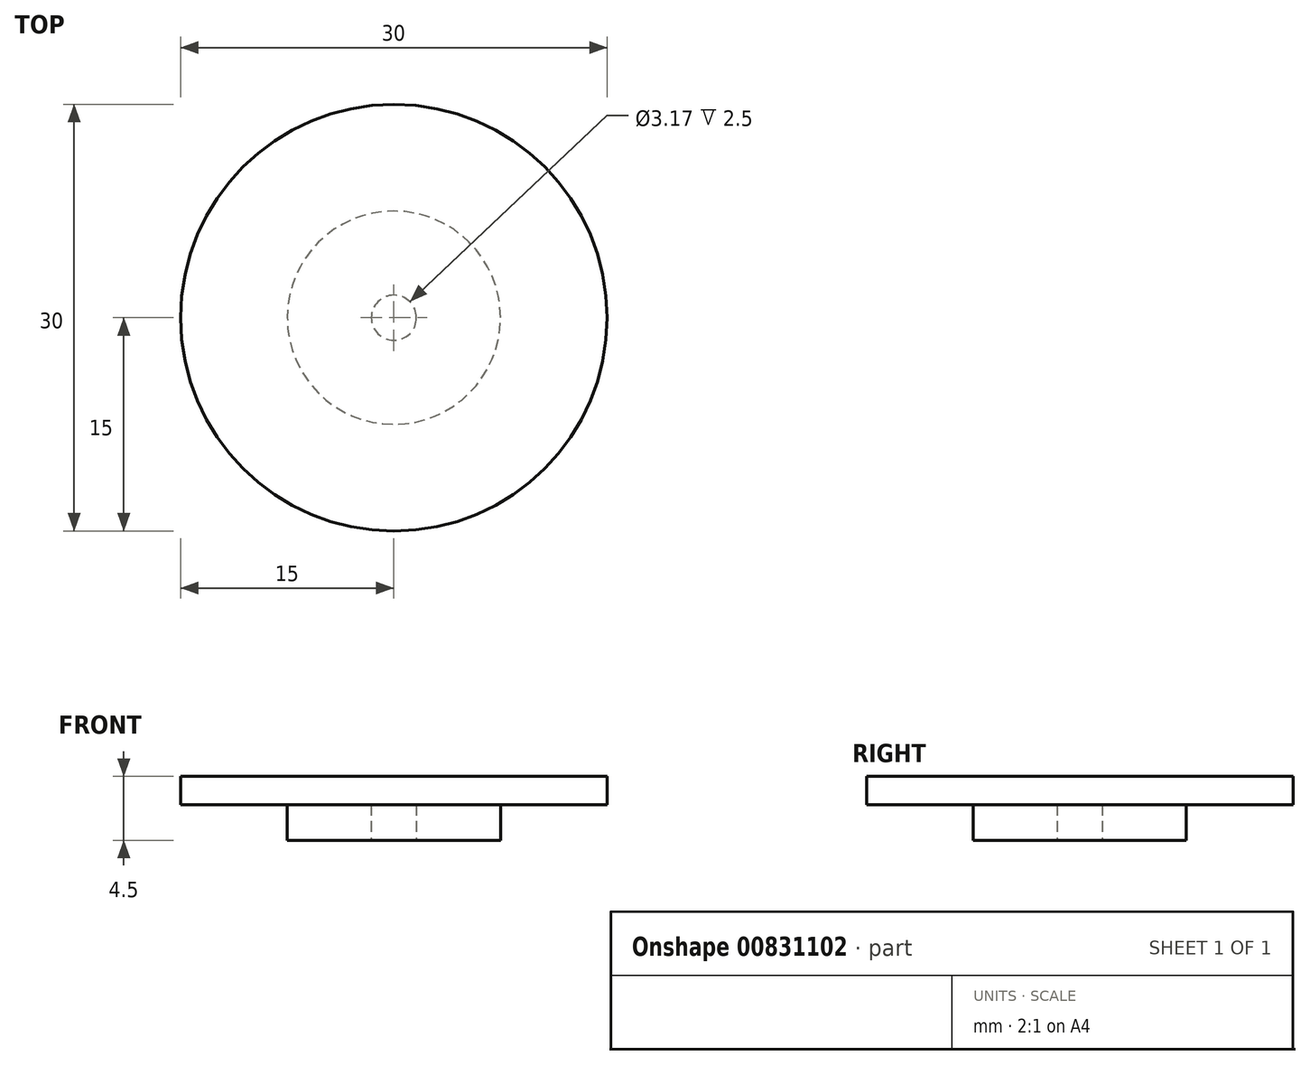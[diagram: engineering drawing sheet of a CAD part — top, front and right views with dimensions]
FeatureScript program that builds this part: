
annotation { "Feature Type Name" : "Feature", "Feature Type Description" : "" }
export const myFeature = defineFeature(function(context is Context, id is Id, definition is map)
    precondition{}
    {
        {
            var Q0;
            Q0=qCreatedBy(makeId("Top.planeOp"),FACE);
            var sketch = newSketch(context, id + "F0", { "sketchPlane" : qUnion([Q0])});
            skCircle(sketch, "E0", {"center": v(0, 0) * mm, "radius": 1.59 * mm});
            skCircle(sketch, "E1", {"center": v(0, 0) * mm, "radius": 7.5 * mm});
            skSolve(sketch);
        }
        {
            var Q0;
            Q0 = qSketchRegion(id + "F0", true);
            var Q1;
            Q1=makeQuery(id+"F0.imprint","IMPRINT",FACE,{"disambiguationData":[TD([[makeQuery(id+"F0.imprint","IMPRINT",EDGE,{"derivedFrom":sQuery(id+"F0.wireOp",EDGE,"E0")}),-1.0]])]});
            extrude(context, id + "F1", {"entities" : qUnion([Q0, Q1]), "depth" : 2.5 * mm, "offsetDistance" : 25.4 * mm});
        }
        {
            var Q0;
            Q0=makeQuery(id+"F1.opExtrude","CAP_FACE",FACE,{"disambiguationData":[OSD([sQuery(id+"F0.wireOp",EDGE,"E0"),sQuery(id+"F0.wireOp",EDGE,"E1")])],"isStart":false});
            var sketch = newSketch(context, id + "F2", { "sketchPlane" : qUnion([Q0])});
            skCircle(sketch, "E2", {"center": v(0, 0) * mm, "radius": 15 * mm});
            skSolve(sketch);
        }
        {
            var Q0;
            Q0 = qSketchRegion(id + "F2", true);
            var Q1;
            Q1=makeQuery(id+"F2.imprint","IMPRINT",FACE,{"disambiguationData":[TD([[makeQuery(id+"F2.imprint","IMPRINT",EDGE,{"derivedFrom":sQuery(id+"F2.wireOp",EDGE,"E2")}),1.0]])]});
            extrude(context, id + "F3", {"entities" : qUnion([Q0, Q1]), "operationType" : NewBodyOperationType.ADD, "depth" : 2 * mm, "offsetDistance" : 25.4 * mm});
        }
    });
